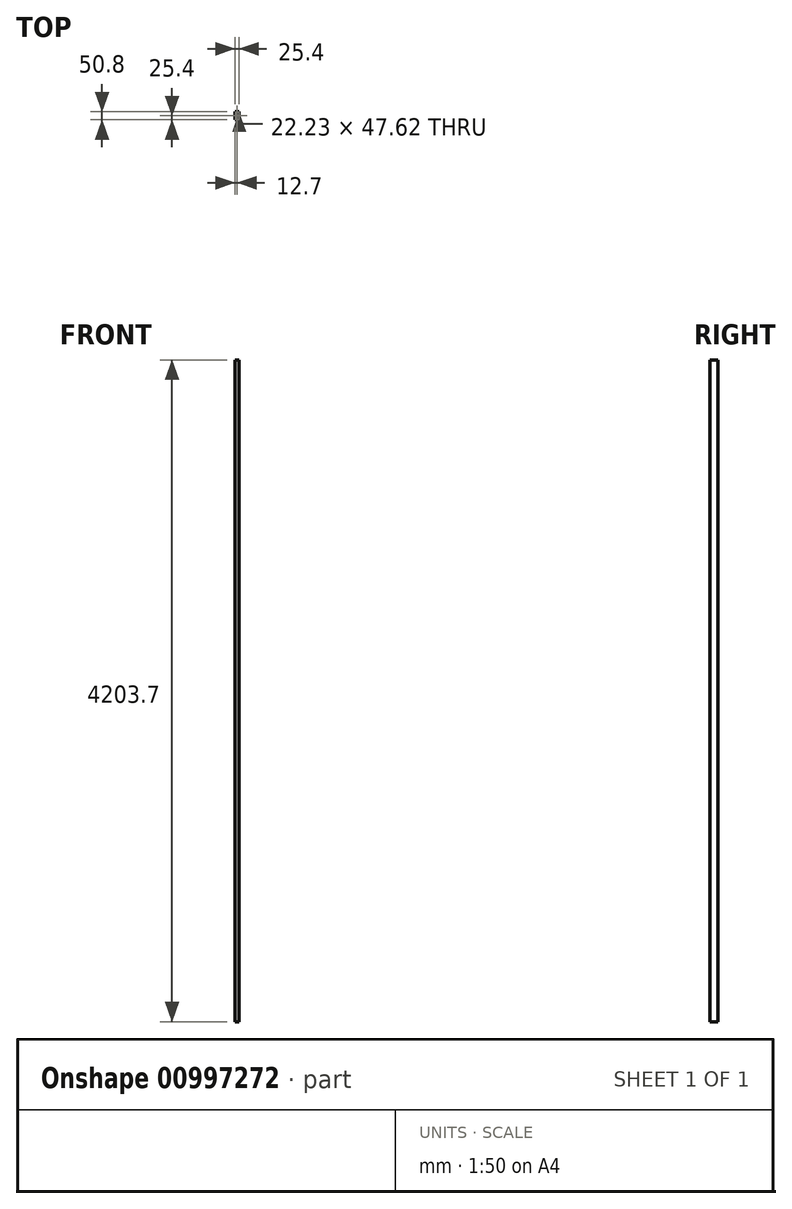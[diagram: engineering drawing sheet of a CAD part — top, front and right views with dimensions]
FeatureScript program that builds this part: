
annotation { "Feature Type Name" : "Feature", "Feature Type Description" : "" }
export const myFeature = defineFeature(function(context is Context, id is Id, definition is map)
    precondition{}
    {
        {
            var Q0;
            Q0=qCreatedBy(makeId("Top.planeOp"),FACE);
            var sketch = newSketch(context, id + "F0", { "sketchPlane" : qUnion([Q0])});
            skLineSegment(sketch, "E0.bottom", {"start": v(-11.11, 23.81) * mm, "end": v(11.11, 23.81) * mm});
            skLineSegment(sketch, "E0.top", {"start": v(-11.11, -23.81) * mm, "end": v(11.11, -23.81) * mm});
            skLineSegment(sketch, "E0.left", {"start": v(-11.11, 23.81) * mm, "end": v(-11.11, -23.81) * mm});
            skLineSegment(sketch, "E0.right", {"start": v(11.11, 23.81) * mm, "end": v(11.11, -23.81) * mm});
            skLineSegment(sketch, "E1.bottom", {"start": v(-12.7, 25.4) * mm, "end": v(12.7, 25.4) * mm});
            skLineSegment(sketch, "E1.top", {"start": v(-12.7, -25.4) * mm, "end": v(12.7, -25.4) * mm});
            skLineSegment(sketch, "E1.left", {"start": v(-12.7, 25.4) * mm, "end": v(-12.7, -25.4) * mm});
            skLineSegment(sketch, "E1.right", {"start": v(12.7, 25.4) * mm, "end": v(12.7, -25.4) * mm});
            skSolve(sketch);
        }
        {
            var Q0;
            Q0 = qSketchRegion(id + "F0", true);
            extrude(context, id + "F1", {"entities" : qUnion([Q0]), "endBound" : BoundingType.SYMMETRIC, "depth" : 4203.7 * mm, "offsetDistance" : 25.4 * mm});
        }
    });
